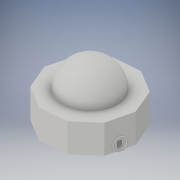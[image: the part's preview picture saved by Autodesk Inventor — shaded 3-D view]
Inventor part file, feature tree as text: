
AUTODESK INVENTOR PART (.ipt)
format: ipt  version: 2017 (Build 210142000, 142)  size: 252,416 bytes
history: native  units: in
note: dims shown in document units (in); Inventor stores cm internally (conversion verified against a paired STEP export)
features: sketch x7, extrude x6, other x3, mirror x1
ambient origin geometry x8: Origin, YZ Plane, XZ Plane, XY Plane, X Axis, Y Axis, Z Axis, Center Point
bodies: Solid1 (feature_tree)
feature tree (17):
  other  "dome"
  extrude  "bace"  Depth=1.0in TaperAngle=0.0deg
  extrude  "bace wall"  Depth=20.0in TaperAngle=0.0deg
  extrude  "bace cieiling"  Depth=6.6667in
  other  "dome work plane"
  extrude  "door frame"  Depth=1.0in TaperAngle=0.0deg
  extrude  "corridor connection"  Depth=0.25in
  extrude  "left door slot"  Depth=2.0in
  other  "door slot mirror"
  mirror  "Mirror1"
  sketch  "Sketch1"  dims[d0=62.0in d1=1.0in d2=0.0in]
  sketch  "Sketch2"  dims[d4=1.0in d5=20.0in d6=0.0in]
  sketch  "Sketch3"  dims[d8=1.0in d9=0.0in d14=6.6667in d15=4.0in]
  sketch  "Sketch7"  dims[d16=2.0in d17=6.6667in d18=1.0in d19=0.0in]
  sketch  "Sketch8"  dims[d20=1.0in d21=0.0in d22=0.25in d23=0.5in d24=6.6667in]
  sketch  "Sketch9"  dims[d25=2.0in d26=0.0in d28=40.0in]
  sketch  "Sketch10"  dims[d32=20.0in d33=21.0in d34=90.0deg]
